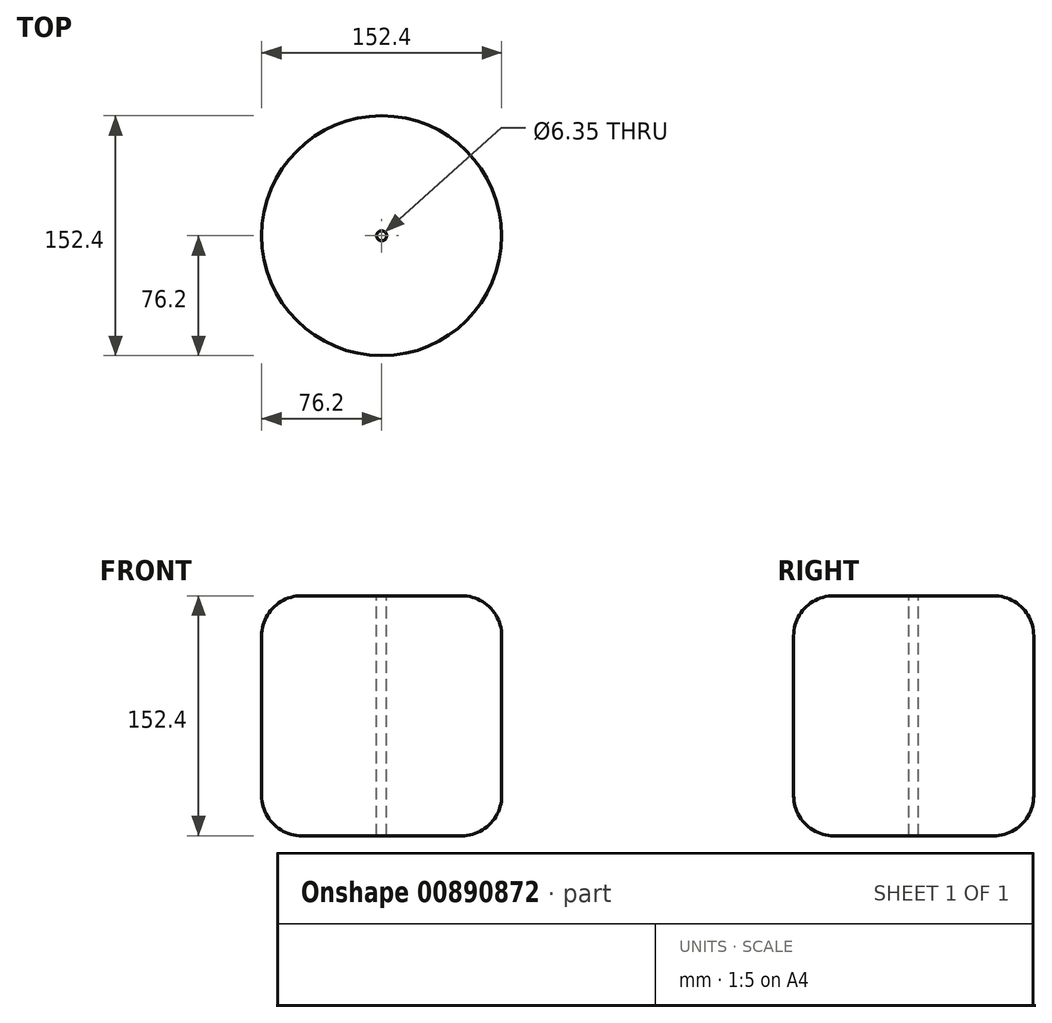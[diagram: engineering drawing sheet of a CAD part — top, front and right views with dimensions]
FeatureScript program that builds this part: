
annotation { "Feature Type Name" : "Feature", "Feature Type Description" : "" }
export const myFeature = defineFeature(function(context is Context, id is Id, definition is map)
    precondition{}
    {
        {
            var Q0;
            Q0=qCreatedBy(makeId("Top.planeOp"),FACE);
            var sketch = newSketch(context, id + "F0", { "sketchPlane" : qUnion([Q0])});
            skCircle(sketch, "E0", {"center": v(0, 0) * mm, "radius": 76.2 * mm});
            skSolve(sketch);
        }
        {
            var Q0;
            Q0=makeQuery(id+"F0.imprint","IMPRINT",FACE,{"disambiguationData":[TD([[makeQuery(id+"F0.imprint","IMPRINT",EDGE,{"derivedFrom":sQuery(id+"F0.wireOp",EDGE,"E0")}),1.0]])]});
            extrude(context, id + "F1", {"entities" : qUnion([Q0]), "depth" : 152.4 * mm, "offsetDistance" : 25.4 * mm});
        }
        {
            var Q0;
            Q0=makeQuery(id+"F1.opExtrude","SWEPT_FACE",FACE,{"disambiguationData":[OSD([sQuery(id+"F0.wireOp",EDGE,"E0")])]});
            fillet(context, id + "F2", {"entities" : qUnion([Q0]), "radius" : 25.4 * mm, "tangentPropagation" : true, "allowEdgeOverflow" : false});
        }
        {
            var Q0;
            Q0=makeQuery(id+"F1.opExtrude","CAP_FACE",FACE,{"disambiguationData":[OSD([sQuery(id+"F0.wireOp",EDGE,"E0")])],"isStart":false});
            var sketch = newSketch(context, id + "F3", { "sketchPlane" : qUnion([Q0])});
            skCircle(sketch, "E1", {"center": v(0, 0) * mm, "radius": 3.18 * mm});
            skSolve(sketch);
        }
        {
            var Q0;
            Q0 = qSketchRegion(id + "F3", true);
            extrude(context, id + "F4", {"entities" : qUnion([Q0]), "operationType" : NewBodyOperationType.REMOVE, "oppositeDirection" : true, "depth" : 254 * mm, "offsetDistance" : 25.4 * mm});
        }
    });
